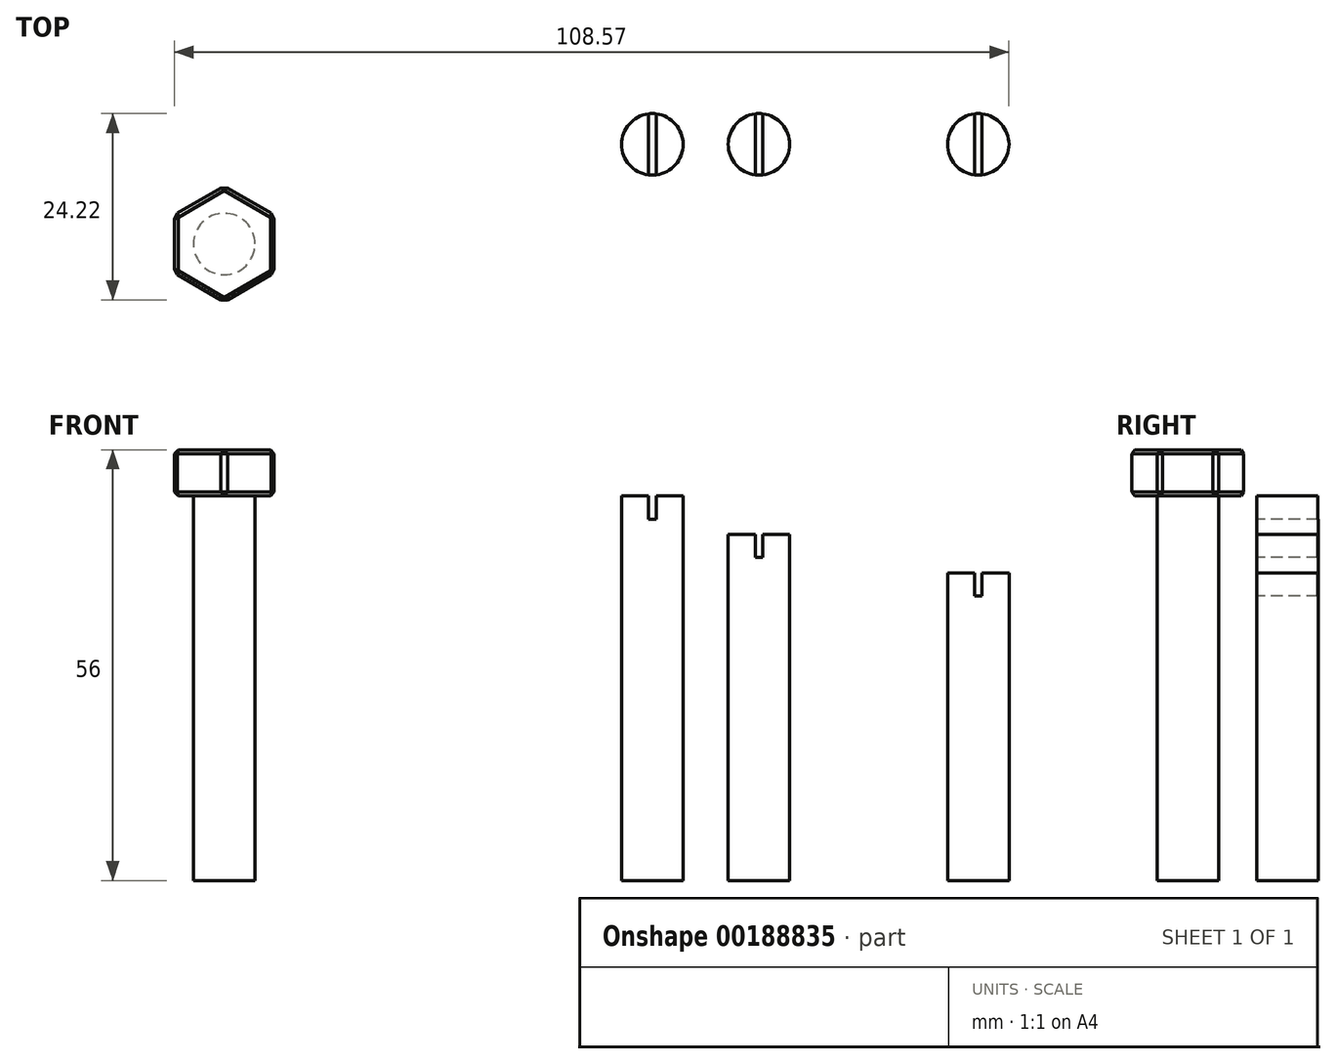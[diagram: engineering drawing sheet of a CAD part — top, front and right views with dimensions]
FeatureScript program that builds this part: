
annotation { "Feature Type Name" : "Feature", "Feature Type Description" : "" }
export const myFeature = defineFeature(function(context is Context, id is Id, definition is map)
    precondition{}
    {
        {
            var Q0;
            Q0=qCreatedBy(makeId("Top.planeOp"),FACE);
            var sketch = newSketch(context, id + "F0", { "sketchPlane" : qUnion([Q0])});
            skCircle(sketch, "E0", {"center": v(0, 0) * mm, "radius": 4 * mm});
            skSolve(sketch);
        }
        {
            var Q0;
            Q0=qSketchRegion(id+"F0",true);
            extrude(context, id + "F1", {"entities" : qUnion([Q0]), "depth" : 50 * mm});
        }
        {
            var Q0;
            Q0=qCreatedBy(makeId("Top.planeOp"),FACE);
            var sketch = newSketch(context, id + "F2", { "sketchPlane" : qUnion([Q0])});
            skCircle(sketch, "E1", {"center": v(42.4, 0) * mm, "radius": 4 * mm});
            skSolve(sketch);
        }
        {
            var Q0;
            Q0=makeQuery(id+"F2.imprint","IMPRINT",FACE,{"disambiguationData":[TD([[makeQuery(id+"F2.imprint","IMPRINT",EDGE,{"derivedFrom":sQuery(id+"F2.wireOp",EDGE,"E1")}),1.0]])]});
            var Q1;
            Q1=sQuery(id+"F2.wireOp",EDGE,"E1");
            extrude(context, id + "F3", {"entities" : qUnion([Q0]), "surfaceEntities" : qUnion([Q1]), "depth" : 40 * mm});
        }
        {
            var Q0;
            Q0=makeQuery(id+"F1.opExtrude","CAP_FACE",FACE,{"disambiguationData":[OSD([sQuery(id+"F0.wireOp",EDGE,"E0")])],"isStart":false});
            var sketch = newSketch(context, id + "F4", { "sketchPlane" : qUnion([Q0])});
            skLineSegment(sketch, "E2.bottom", {"start": v(0.5, 4) * mm, "end": v(-0.5, 4) * mm});
            skLineSegment(sketch, "E2.top", {"start": v(0.5, -4) * mm, "end": v(-0.5, -4) * mm});
            skLineSegment(sketch, "E2.left", {"start": v(0.5, 4) * mm, "end": v(0.5, -4) * mm});
            skLineSegment(sketch, "E2.right", {"start": v(-0.5, 4) * mm, "end": v(-0.5, -4) * mm});
            skPoint(sketch, "E2.middle", {"position": v(0, 0) * mm});
            skSolve(sketch);
        }
        {
            var Q0;
            {var subQ0=makeQuery(id+"F1.opExtrude","CAP_EDGE",EDGE,{"disambiguationData":[OSD([sQuery(id+"F0.wireOp",EDGE,"E0")])],"isStart":false});var subQ4=sQuery(id+"F4.wireOp",EDGE,"E2.left");var subQ5=makeQuery(id+"F4.imprint","INTERSECT",VERTEX,{"disambiguationData":[OD(0.0)],"derivedFrom":[subQ0,subQ4]});Q0=makeQuery(id+"F4.imprint","IMPRINT",FACE,{"disambiguationData":[TD([[makeQuery(id+"F4.imprint","IMPRINT",EDGE,{"disambiguationData":[TD([[subQ5,-1.0]])],"derivedFrom":subQ4}),-1.0]])]});}
            extrude(context, id + "F5", {"entities" : qUnion([Q0]), "operationType" : NewBodyOperationType.REMOVE, "oppositeDirection" : true, "depth" : 3 * mm});
        }
        {
            var Q0;
            Q0=makeQuery(id+"F3.opExtrude","CAP_FACE",FACE,{"disambiguationData":[OSD([sQuery(id+"F2.wireOp",EDGE,"E1")])],"isStart":false});
            var sketch = newSketch(context, id + "F6", { "sketchPlane" : qUnion([Q0])});
            skLineSegment(sketch, "E3.bottom", {"start": v(42.9, 4) * mm, "end": v(41.9, 4) * mm});
            skLineSegment(sketch, "E3.top", {"start": v(42.9, -4) * mm, "end": v(41.9, -4) * mm});
            skLineSegment(sketch, "E3.left", {"start": v(42.9, 4) * mm, "end": v(42.9, -4) * mm});
            skLineSegment(sketch, "E3.right", {"start": v(41.9, 4) * mm, "end": v(41.9, -4) * mm});
            skPoint(sketch, "E3.middle", {"position": v(42.4, 0) * mm});
            skSolve(sketch);
        }
        {
            var Q0;
            {var subQ0=makeQuery(id+"F3.opExtrude","CAP_EDGE",EDGE,{"disambiguationData":[OSD([sQuery(id+"F2.wireOp",EDGE,"E1")])],"isStart":false});var subQ5=sQuery(id+"F6.wireOp",EDGE,"E3.left");var subQ6=makeQuery(id+"F6.imprint","INTERSECT",VERTEX,{"disambiguationData":[OD(0.0)],"derivedFrom":[subQ0,subQ5]});Q0=makeQuery(id+"F6.imprint","IMPRINT",FACE,{"disambiguationData":[TD([[makeQuery(id+"F6.imprint","IMPRINT",EDGE,{"disambiguationData":[TD([[subQ6,-1.0]])],"derivedFrom":subQ5}),-1.0]])]});}
            extrude(context, id + "F7", {"entities" : qUnion([Q0]), "operationType" : NewBodyOperationType.REMOVE, "oppositeDirection" : true, "depth" : 3 * mm});
        }
        {
            var Q0;
            Q0=qCreatedBy(makeId("Top.planeOp"),FACE);
            var sketch = newSketch(context, id + "F8", { "sketchPlane" : qUnion([Q0])});
            skCircle(sketch, "E4", {"center": v(13.88, 0) * mm, "radius": 4 * mm});
            skSolve(sketch);
        }
        {
            var Q0;
            Q0=makeQuery(id+"F8.imprint","IMPRINT",FACE,{"disambiguationData":[TD([[makeQuery(id+"F8.imprint","IMPRINT",EDGE,{"derivedFrom":sQuery(id+"F8.wireOp",EDGE,"E4")}),1.0]])]});
            var Q1;
            Q1=sQuery(id+"F8.wireOp",EDGE,"E4");
            extrude(context, id + "F9", {"entities" : qUnion([Q0]), "surfaceEntities" : qUnion([Q1]), "depth" : 45 * mm});
        }
        {
            var Q0;
            Q0=makeQuery(id+"F9.opExtrude","CAP_FACE",FACE,{"disambiguationData":[OSD([sQuery(id+"F8.wireOp",EDGE,"E4")])],"isStart":false});
            var sketch = newSketch(context, id + "F10", { "sketchPlane" : qUnion([Q0])});
            skLineSegment(sketch, "E5.bottom", {"start": v(14.38, 4) * mm, "end": v(13.38, 4) * mm});
            skLineSegment(sketch, "E5.top", {"start": v(14.38, -4) * mm, "end": v(13.38, -4) * mm});
            skLineSegment(sketch, "E5.left", {"start": v(14.38, 4) * mm, "end": v(14.38, -4) * mm});
            skLineSegment(sketch, "E5.right", {"start": v(13.38, 4) * mm, "end": v(13.38, -4) * mm});
            skPoint(sketch, "E5.middle", {"position": v(13.88, 0) * mm});
            skSolve(sketch);
        }
        {
            var Q0;
            {var subQ0=makeQuery(id+"F9.opExtrude","CAP_EDGE",EDGE,{"disambiguationData":[OSD([sQuery(id+"F8.wireOp",EDGE,"E4")])],"isStart":false});var subQ4=sQuery(id+"F10.wireOp",EDGE,"E5.left");var subQ5=makeQuery(id+"F10.imprint","INTERSECT",VERTEX,{"disambiguationData":[OD(0.0)],"derivedFrom":[subQ0,subQ4]});Q0=makeQuery(id+"F10.imprint","IMPRINT",FACE,{"disambiguationData":[TD([[makeQuery(id+"F10.imprint","IMPRINT",EDGE,{"disambiguationData":[TD([[subQ5,-1.0]])],"derivedFrom":subQ4}),-1.0]])]});}
            extrude(context, id + "F11", {"entities" : qUnion([Q0]), "operationType" : NewBodyOperationType.REMOVE, "oppositeDirection" : true, "depth" : 3 * mm});
        }
        {
            var Q0;
            Q0=qCreatedBy(makeId("Top.planeOp"),FACE);
            var sketch = newSketch(context, id + "F12", { "sketchPlane" : qUnion([Q0])});
            skCircle(sketch, "E6", {"center": v(-55.68, -12.96) * mm, "radius": 4 * mm});
            skSolve(sketch);
        }
        {
            var Q0;
            Q0=makeQuery(id+"F12.imprint","IMPRINT",FACE,{"disambiguationData":[TD([[makeQuery(id+"F12.imprint","IMPRINT",EDGE,{"derivedFrom":sQuery(id+"F12.wireOp",EDGE,"E6")}),1.0]])]});
            extrude(context, id + "F13", {"entities" : qUnion([Q0]), "depth" : 50 * mm});
        }
        {
            var Q0;
            Q0=makeQuery(id+"F13.opExtrude","CAP_FACE",FACE,{"disambiguationData":[OSD([sQuery(id+"F12.wireOp",EDGE,"E6")])],"isStart":false});
            var sketch = newSketch(context, id + "F14", { "sketchPlane" : qUnion([Q0])});
            skCircle(sketch, "E7.cCircle", {"center": v(-55.68, -12.96) * mm, "radius": 6.5 * mm, "construction": true});
            skLineSegment(sketch, "E7.0", {"start": v(-49.18, -9.2) * mm, "end": v(-49.18, -16.72) * mm});
            skLineSegment(sketch, "E7.1", {"start": v(-49.18, -16.72) * mm, "end": v(-55.68, -20.47) * mm});
            skLineSegment(sketch, "E7.2", {"start": v(-55.68, -20.47) * mm, "end": v(-62.18, -16.72) * mm});
            skLineSegment(sketch, "E7.3", {"start": v(-62.18, -16.72) * mm, "end": v(-62.18, -9.2) * mm});
            skLineSegment(sketch, "E7.4", {"start": v(-62.18, -9.2) * mm, "end": v(-55.68, -5.46) * mm});
            skLineSegment(sketch, "E7.5", {"start": v(-55.68, -5.46) * mm, "end": v(-49.18, -9.2) * mm});
            skPoint(sketch, "E7.0.midPoint", {"position": v(-49.18, -12.96) * mm});
            skSolve(sketch);
        }
        {
            var Q0;
            Q0 = qSketchRegion(id + "F14", true);
            extrude(context, id + "F15", {"entities" : qUnion([Q0]), "operationType" : NewBodyOperationType.ADD, "depth" : 6 * mm});
        }
        {
            var Q0;
            Q0=makeQuery(id+"F15.opExtrude","CAP_FACE",FACE,{"disambiguationData":[OSD([sQuery(id+"F14.wireOp",EDGE,"E7.0"),sQuery(id+"F14.wireOp",EDGE,"E7.1"),sQuery(id+"F14.wireOp",EDGE,"E7.2"),sQuery(id+"F14.wireOp",EDGE,"E7.3"),sQuery(id+"F14.wireOp",EDGE,"E7.4"),sQuery(id+"F14.wireOp",EDGE,"E7.5")])],"isStart":false});
            var Q1;
            Q1=makeQuery(id+"F15.opExtrude","SWEPT_FACE",FACE,{"disambiguationData":[OSD([sQuery(id+"F14.wireOp",EDGE,"E7.1")])]});
            var Q2;
            Q2=makeQuery(id+"F15.opExtrude","SWEPT_FACE",FACE,{"disambiguationData":[OSD([sQuery(id+"F14.wireOp",EDGE,"E7.2")])]});
            var Q3;
            Q3=makeQuery(id+"F15.opExtrude","SWEPT_FACE",FACE,{"disambiguationData":[OSD([sQuery(id+"F14.wireOp",EDGE,"E7.0")])]});
            var Q4;
            Q4=makeQuery(id+"F15.opExtrude","SWEPT_FACE",FACE,{"disambiguationData":[OSD([sQuery(id+"F14.wireOp",EDGE,"E7.5")])]});
            var Q5;
            Q5=makeQuery(id+"F15.opExtrude","SWEPT_FACE",FACE,{"disambiguationData":[OSD([sQuery(id+"F14.wireOp",EDGE,"E7.4")])]});
            var Q6;
            Q6=makeQuery(id+"F15.opExtrude","SWEPT_FACE",FACE,{"disambiguationData":[OSD([sQuery(id+"F14.wireOp",EDGE,"E7.3")])]});
            chamfer(context, id + "F16", {"entities" : qUnion([Q0, Q1, Q2, Q3, Q4, Q5, Q6]), "width" : .5 * mm, "tangentPropagation" : true});
        }
    });
